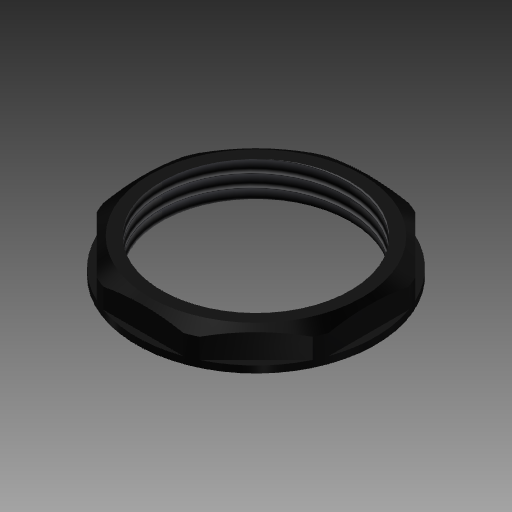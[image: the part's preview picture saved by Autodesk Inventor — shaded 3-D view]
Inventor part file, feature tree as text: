
AUTODESK INVENTOR PART (.ipt)
format: ipt  version: 2017.1 (Build 211199000, 199)  size: 140,288 bytes
history: native  units: mm
features: imported_body x1, thread x1
ambient origin geometry x8: Origin, YZ Plane, XZ Plane, XY Plane, X Axis, Y Axis, Z Axis, Center Point
bodies: Solid1 (feature_tree)
feature tree (2):
  imported_body  "Base1"
  thread  "Thread1"  [1 undecoded]
note: 1 required parameter value undecoded (feature->parameter linkage not recoverable at this tier; creation-order binding heuristic only, values carry confidence <= 0.55)
